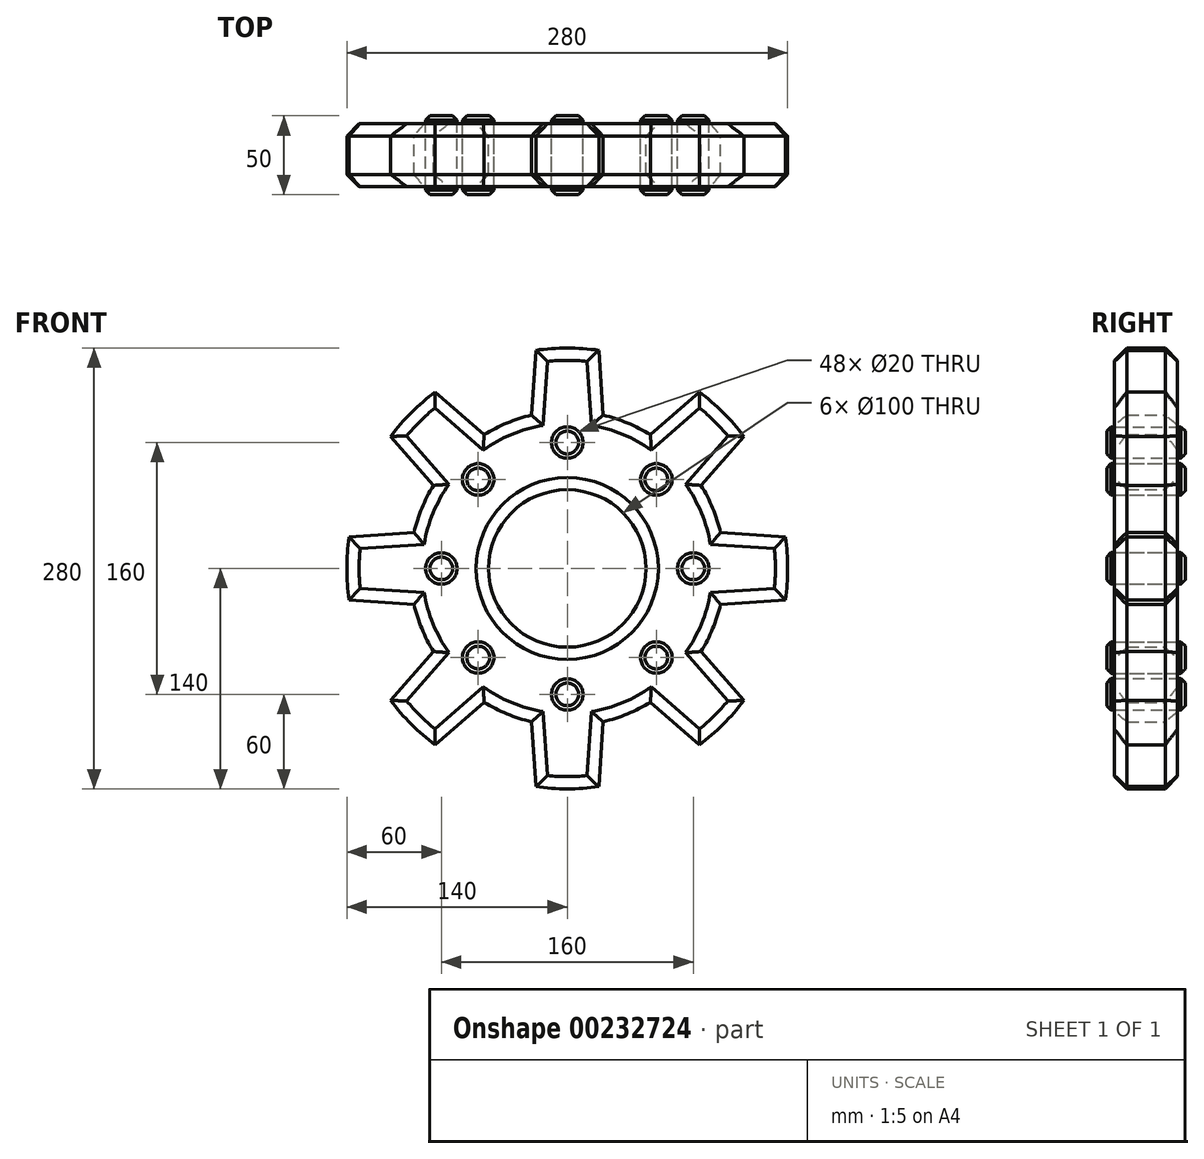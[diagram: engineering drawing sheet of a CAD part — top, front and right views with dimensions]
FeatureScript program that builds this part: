
annotation { "Feature Type Name" : "Feature", "Feature Type Description" : "" }
export const myFeature = defineFeature(function(context is Context, id is Id, definition is map)
    precondition{}
    {
        {
            var Q0;
            Q0=qCreatedBy(makeId("Front.planeOp"),FACE);
            var sketch = newSketch(context, id + "F0", { "sketchPlane" : qUnion([Q0])});
            skLineSegment(sketch, "E0.bottom", {"start": v(-160, 160) * mm, "end": v(160, 160) * mm});
            skLineSegment(sketch, "E0.top", {"start": v(-160, -160) * mm, "end": v(160, -160) * mm});
            skLineSegment(sketch, "E0.left", {"start": v(-160, 160) * mm, "end": v(-160, -160) * mm});
            skLineSegment(sketch, "E0.right", {"start": v(160, 160) * mm, "end": v(160, -160) * mm});
            skPoint(sketch, "E0.middle", {"position": v(0, 0) * mm});
            skLineSegment(sketch, "E1.bottom", {"start": v(-40, 160) * mm, "end": v(40, 160) * mm});
            skLineSegment(sketch, "E1.top", {"start": v(-40, -160) * mm, "end": v(40, -160) * mm});
            skLineSegment(sketch, "E1.left", {"start": v(-40, 160) * mm, "end": v(-40, -160) * mm});
            skLineSegment(sketch, "E1.right", {"start": v(40, 160) * mm, "end": v(40, -160) * mm});
            skLineSegment(sketch, "E2.bottom", {"start": v(-20, 160) * mm, "end": v(20, 160) * mm});
            skLineSegment(sketch, "E2.top", {"start": v(-20, -160) * mm, "end": v(20, -160) * mm});
            skLineSegment(sketch, "E2.left", {"start": v(-20, 160) * mm, "end": v(-20, -160) * mm});
            skLineSegment(sketch, "E2.right", {"start": v(20, 160) * mm, "end": v(20, -160) * mm});
            skLineSegment(sketch, "E3.bottom", {"start": v(-160, 40) * mm, "end": v(160, 40) * mm});
            skLineSegment(sketch, "E3.top", {"start": v(-160, -40) * mm, "end": v(160, -40) * mm});
            skLineSegment(sketch, "E3.left", {"start": v(-160, 40) * mm, "end": v(-160, -40) * mm});
            skLineSegment(sketch, "E3.right", {"start": v(160, 40) * mm, "end": v(160, -40) * mm});
            skLineSegment(sketch, "E4.bottom", {"start": v(-160, 20) * mm, "end": v(160, 20) * mm});
            skLineSegment(sketch, "E4.top", {"start": v(-160, -20) * mm, "end": v(160, -20) * mm});
            skLineSegment(sketch, "E4.left", {"start": v(-160, 20) * mm, "end": v(-160, -20) * mm});
            skLineSegment(sketch, "E4.right", {"start": v(160, 20) * mm, "end": v(160, -20) * mm});
            skLineSegment(sketch, "E5", {"start": v(-160, 160) * mm, "end": v(160, -160) * mm});
            skLineSegment(sketch, "E6", {"start": v(-160, -160) * mm, "end": v(160, 160) * mm});
            skLineSegment(sketch, "E7", {"start": v(-84.85, 141.42) * mm, "end": v(-113.14, 113.14) * mm});
            skLineSegment(sketch, "E8", {"start": v(-113.14, 113.14) * mm, "end": v(-141.42, 84.85) * mm});
            skLineSegment(sketch, "E9", {"start": v(0, 0) * mm, "end": v(-113.14, 113.14) * mm});
            skLineSegment(sketch, "E10", {"start": v(84.85, -141.42) * mm, "end": v(113.14, -113.14) * mm});
            skLineSegment(sketch, "E11", {"start": v(113.14, -113.14) * mm, "end": v(141.42, -84.85) * mm});
            skLineSegment(sketch, "E12", {"start": v(0, 0) * mm, "end": v(113.14, -113.14) * mm});
            skPoint(sketch, "E13", {"position": v(-99, 127.28) * mm});
            skPoint(sketch, "E14", {"position": v(-127.28, 99) * mm});
            skPoint(sketch, "E15", {"position": v(127.28, -99) * mm});
            skPoint(sketch, "E16", {"position": v(99, -127.28) * mm});
            skLineSegment(sketch, "E17", {"start": v(-127.28, 99) * mm, "end": v(99, -127.28) * mm});
            skLineSegment(sketch, "E18", {"start": v(-99, 127.28) * mm, "end": v(127.28, -99) * mm});
            skLineSegment(sketch, "E19", {"start": v(-160, 0) * mm, "end": v(160, 0) * mm});
            skLineSegment(sketch, "E20", {"start": v(0, 160) * mm, "end": v(0, -160) * mm});
            skLineSegment(sketch, "E21", {"start": v(84.85, 141.42) * mm, "end": v(113.14, 113.14) * mm});
            skLineSegment(sketch, "E22", {"start": v(113.14, 113.14) * mm, "end": v(141.42, 84.85) * mm});
            skPoint(sketch, "E23", {"position": v(99, 127.28) * mm});
            skPoint(sketch, "E24", {"position": v(127.28, 99) * mm});
            skLineSegment(sketch, "E25", {"start": v(-141.42, -84.85) * mm, "end": v(-113.14, -113.14) * mm});
            skLineSegment(sketch, "E26", {"start": v(-113.14, -113.14) * mm, "end": v(-84.85, -141.42) * mm});
            skPoint(sketch, "E27", {"position": v(-127.28, -99) * mm});
            skPoint(sketch, "E28", {"position": v(-99, -127.28) * mm});
            skLineSegment(sketch, "E29", {"start": v(-127.28, -99) * mm, "end": v(99, 127.28) * mm});
            skLineSegment(sketch, "E30", {"start": v(-99, -127.28) * mm, "end": v(127.28, 99) * mm});
            skCircle(sketch, "E31", {"center": v(0, 0) * mm, "radius": 80 * mm});
            skPoint(sketch, "E32", {"position": v(0, 80) * mm});
            skPoint(sketch, "E33", {"position": v(56.57, 56.57) * mm});
            skPoint(sketch, "E34", {"position": v(-56.57, 56.57) * mm});
            skPoint(sketch, "E35", {"position": v(-80, 0) * mm});
            skPoint(sketch, "E36", {"position": v(80, 0) * mm});
            skPoint(sketch, "E37", {"position": v(0, -80) * mm});
            skPoint(sketch, "E38", {"position": v(-56.57, -56.57) * mm});
            skPoint(sketch, "E39", {"position": v(56.57, -56.57) * mm});
            skSolve(sketch);
        }
        {
            var Q0;
            Q0=qCreatedBy(makeId("Front.planeOp"),FACE);
            var sketch = newSketch(context, id + "F1", { "sketchPlane" : qUnion([Q0])});
            skCircle(sketch, "E40", {"center": v(0, 0) * mm, "radius": 50 * mm});
            skArc(sketch, "E41", {"start": v(20, 138.56) * mm, "mid": v(0, 140) * mm, "end": v(-20, 138.56) * mm});
            skArc(sketch, "E42", {"start": v(-83.84, 112.12) * mm, "mid": v(-99, 99) * mm, "end": v(-112.12, 83.84) * mm});
            skArc(sketch, "E43", {"start": v(-138.56, 20) * mm, "mid": v(-140, 0) * mm, "end": v(-138.56, -20) * mm});
            skArc(sketch, "E44", {"start": v(-112.12, -83.84) * mm, "mid": v(-99, -99) * mm, "end": v(-83.84, -112.12) * mm});
            skArc(sketch, "E45", {"start": v(-20, -138.56) * mm, "mid": v(0, -140) * mm, "end": v(20, -138.56) * mm});
            skArc(sketch, "E46", {"start": v(83.84, -112.12) * mm, "mid": v(99, -99) * mm, "end": v(112.12, -83.84) * mm});
            skArc(sketch, "E47", {"start": v(138.56, -20) * mm, "mid": v(140, 0) * mm, "end": v(138.56, 20) * mm});
            skArc(sketch, "E48", {"start": v(112.12, 83.84) * mm, "mid": v(99, 99) * mm, "end": v(83.84, 112.12) * mm});
            skLineSegment(sketch, "E49", {"start": v(-20, 138.56) * mm, "end": v(-22.76, 97.38) * mm});
            skLineSegment(sketch, "E50", {"start": v(20, 138.56) * mm, "end": v(22.76, 97.38) * mm});
            skArc(sketch, "E51", {"start": v(-22.76, 97.38) * mm, "mid": v(-38.27, 92.39) * mm, "end": v(-52.76, 84.95) * mm});
            skLineSegment(sketch, "E52", {"start": v(-112.12, 83.84) * mm, "end": v(-84.95, 52.76) * mm});
            skLineSegment(sketch, "E53", {"start": v(-83.84, 112.12) * mm, "end": v(-52.76, 84.95) * mm});
            skArc(sketch, "E54", {"start": v(-84.95, 52.76) * mm, "mid": v(-92.39, 38.27) * mm, "end": v(-97.38, 22.76) * mm});
            skLineSegment(sketch, "E55", {"start": v(-138.56, 20) * mm, "end": v(-97.38, 22.76) * mm});
            skLineSegment(sketch, "E56", {"start": v(-138.56, -20) * mm, "end": v(-97.38, -22.76) * mm});
            skArc(sketch, "E57", {"start": v(-97.38, -22.76) * mm, "mid": v(-92.39, -38.27) * mm, "end": v(-84.95, -52.76) * mm});
            skLineSegment(sketch, "E58", {"start": v(-112.12, -83.84) * mm, "end": v(-84.95, -52.76) * mm});
            skLineSegment(sketch, "E59", {"start": v(-83.84, -112.12) * mm, "end": v(-52.76, -84.95) * mm});
            skArc(sketch, "E60", {"start": v(-52.76, -84.95) * mm, "mid": v(-38.27, -92.39) * mm, "end": v(-22.76, -97.38) * mm});
            skLineSegment(sketch, "E61", {"start": v(-20, -138.56) * mm, "end": v(-22.76, -97.38) * mm});
            skLineSegment(sketch, "E62", {"start": v(20, -138.56) * mm, "end": v(22.76, -97.38) * mm});
            skArc(sketch, "E63", {"start": v(22.76, -97.38) * mm, "mid": v(38.27, -92.39) * mm, "end": v(52.76, -84.95) * mm});
            skLineSegment(sketch, "E64", {"start": v(138.56, 20) * mm, "end": v(97.38, 22.76) * mm});
            skLineSegment(sketch, "E65", {"start": v(138.56, -20) * mm, "end": v(97.38, -22.76) * mm});
            skArc(sketch, "E66", {"start": v(97.38, 22.76) * mm, "mid": v(92.39, 38.27) * mm, "end": v(84.95, 52.76) * mm});
            skLineSegment(sketch, "E67", {"start": v(83.84, 112.12) * mm, "end": v(52.76, 84.95) * mm});
            skLineSegment(sketch, "E68", {"start": v(112.12, 83.84) * mm, "end": v(84.95, 52.76) * mm});
            skArc(sketch, "E69", {"start": v(52.76, 84.95) * mm, "mid": v(38.27, 92.39) * mm, "end": v(22.76, 97.38) * mm});
            skLineSegment(sketch, "E70", {"start": v(112.12, -83.84) * mm, "end": v(84.95, -52.76) * mm});
            skLineSegment(sketch, "E71", {"start": v(83.84, -112.12) * mm, "end": v(52.76, -84.95) * mm});
            skArc(sketch, "E72", {"start": v(84.95, -52.76) * mm, "mid": v(92.39, -38.27) * mm, "end": v(97.38, -22.76) * mm});
            skCircle(sketch, "E73", {"center": v(0, 80) * mm, "radius": 10 * mm});
            skCircle(sketch, "E74", {"center": v(56.57, 56.57) * mm, "radius": 10 * mm});
            skCircle(sketch, "E75", {"center": v(-56.57, 56.57) * mm, "radius": 10 * mm});
            skCircle(sketch, "E76", {"center": v(-80, 0) * mm, "radius": 10 * mm});
            skCircle(sketch, "E77", {"center": v(-56.57, -56.57) * mm, "radius": 10 * mm});
            skCircle(sketch, "E78", {"center": v(0, -80) * mm, "radius": 10 * mm});
            skCircle(sketch, "E79", {"center": v(56.57, -56.57) * mm, "radius": 10 * mm});
            skCircle(sketch, "E80", {"center": v(80, 0) * mm, "radius": 10 * mm});
            skSolve(sketch);
        }
        {
            var Q0;
            Q0=makeQuery(id+"F1.imprint","IMPRINT",FACE,{"disambiguationData":[TD([[makeQuery(id+"F1.imprint","IMPRINT",EDGE,{"derivedFrom":sQuery(id+"F1.wireOp",EDGE,"E40")}),-1.0]])]});
            extrude(context, id + "F2", {"entities" : qUnion([Q0]), "endBound" : BoundingType.SYMMETRIC, "depth" : 40 * mm});
        }
        {
            var Q0;
            Q0=makeQuery(id+"F1.imprint","IMPRINT",FACE,{"disambiguationData":[TD([[makeQuery(id+"F1.imprint","IMPRINT",EDGE,{"derivedFrom":sQuery(id+"F1.wireOp",EDGE,"E75")}),1.0]])]});
            var Q1;
            Q1=makeQuery(id+"F1.imprint","IMPRINT",FACE,{"disambiguationData":[TD([[makeQuery(id+"F1.imprint","IMPRINT",EDGE,{"derivedFrom":sQuery(id+"F1.wireOp",EDGE,"E76")}),1.0]])]});
            var Q2;
            Q2=makeQuery(id+"F1.imprint","IMPRINT",FACE,{"disambiguationData":[TD([[makeQuery(id+"F1.imprint","IMPRINT",EDGE,{"derivedFrom":sQuery(id+"F1.wireOp",EDGE,"E77")}),1.0]])]});
            var Q3;
            Q3=makeQuery(id+"F1.imprint","IMPRINT",FACE,{"disambiguationData":[TD([[makeQuery(id+"F1.imprint","IMPRINT",EDGE,{"derivedFrom":sQuery(id+"F1.wireOp",EDGE,"E78")}),1.0]])]});
            var Q4;
            Q4=makeQuery(id+"F1.imprint","IMPRINT",FACE,{"disambiguationData":[TD([[makeQuery(id+"F1.imprint","IMPRINT",EDGE,{"derivedFrom":sQuery(id+"F1.wireOp",EDGE,"E79")}),1.0]])]});
            var Q5;
            Q5=makeQuery(id+"F1.imprint","IMPRINT",FACE,{"disambiguationData":[TD([[makeQuery(id+"F1.imprint","IMPRINT",EDGE,{"derivedFrom":sQuery(id+"F1.wireOp",EDGE,"E80")}),1.0]])]});
            var Q6;
            Q6=makeQuery(id+"F1.imprint","IMPRINT",FACE,{"disambiguationData":[TD([[makeQuery(id+"F1.imprint","IMPRINT",EDGE,{"derivedFrom":sQuery(id+"F1.wireOp",EDGE,"E74")}),1.0]])]});
            var Q7;
            Q7=makeQuery(id+"F1.imprint","IMPRINT",FACE,{"disambiguationData":[TD([[makeQuery(id+"F1.imprint","IMPRINT",EDGE,{"derivedFrom":sQuery(id+"F1.wireOp",EDGE,"E73")}),1.0]])]});
            extrude(context, id + "F3", {"entities" : qUnion([Q0, Q1, Q2, Q3, Q4, Q5, Q6, Q7]), "endBound" : BoundingType.SYMMETRIC, "depth" : 50 * mm});
        }
        {
            var Q0;
            Q0=makeQuery(id+"F2.opExtrude","CAP_EDGE",EDGE,{"disambiguationData":[OSD([sQuery(id+"F1.wireOp",EDGE,"E41")])],"isStart":false});
            var Q1;
            Q1=makeQuery(id+"F2.opExtrude","CAP_EDGE",EDGE,{"disambiguationData":[OSD([sQuery(id+"F1.wireOp",EDGE,"E49")])],"isStart":false});
            var Q2;
            Q2=makeQuery(id+"F2.opExtrude","CAP_EDGE",EDGE,{"disambiguationData":[OSD([sQuery(id+"F1.wireOp",EDGE,"E50")])],"isStart":false});
            var Q3;
            Q3=makeQuery(id+"F2.opExtrude","CAP_EDGE",EDGE,{"disambiguationData":[OSD([sQuery(id+"F1.wireOp",EDGE,"E69")])],"isStart":false});
            var Q4;
            Q4=makeQuery(id+"F2.opExtrude","CAP_EDGE",EDGE,{"disambiguationData":[OSD([sQuery(id+"F1.wireOp",EDGE,"E67")])],"isStart":false});
            var Q5;
            Q5=makeQuery(id+"F2.opExtrude","CAP_EDGE",EDGE,{"disambiguationData":[OSD([sQuery(id+"F1.wireOp",EDGE,"E68")])],"isStart":false});
            var Q6;
            Q6=makeQuery(id+"F2.opExtrude","CAP_EDGE",EDGE,{"disambiguationData":[OSD([sQuery(id+"F1.wireOp",EDGE,"E66")])],"isStart":false});
            var Q7;
            Q7=makeQuery(id+"F2.opExtrude","CAP_EDGE",EDGE,{"disambiguationData":[OSD([sQuery(id+"F1.wireOp",EDGE,"E64")])],"isStart":false});
            var Q8;
            Q8=makeQuery(id+"F2.opExtrude","CAP_EDGE",EDGE,{"disambiguationData":[OSD([sQuery(id+"F1.wireOp",EDGE,"E47")])],"isStart":false});
            var Q9;
            Q9=makeQuery(id+"F2.opExtrude","CAP_EDGE",EDGE,{"disambiguationData":[OSD([sQuery(id+"F1.wireOp",EDGE,"E48")])],"isStart":false});
            var Q10;
            Q10=makeQuery(id+"F2.opExtrude","CAP_EDGE",EDGE,{"disambiguationData":[OSD([sQuery(id+"F1.wireOp",EDGE,"E65")])],"isStart":false});
            var Q11;
            Q11=makeQuery(id+"F2.opExtrude","CAP_EDGE",EDGE,{"disambiguationData":[OSD([sQuery(id+"F1.wireOp",EDGE,"E72")])],"isStart":false});
            var Q12;
            Q12=makeQuery(id+"F2.opExtrude","CAP_EDGE",EDGE,{"disambiguationData":[OSD([sQuery(id+"F1.wireOp",EDGE,"E46")])],"isStart":false});
            var Q13;
            Q13=makeQuery(id+"F2.opExtrude","CAP_EDGE",EDGE,{"disambiguationData":[OSD([sQuery(id+"F1.wireOp",EDGE,"E71")])],"isStart":false});
            var Q14;
            Q14=makeQuery(id+"F2.opExtrude","CAP_EDGE",EDGE,{"disambiguationData":[OSD([sQuery(id+"F1.wireOp",EDGE,"E63")])],"isStart":false});
            var Q15;
            Q15=makeQuery(id+"F2.opExtrude","CAP_EDGE",EDGE,{"disambiguationData":[OSD([sQuery(id+"F1.wireOp",EDGE,"E62")])],"isStart":false});
            var Q16;
            Q16=makeQuery(id+"F2.opExtrude","CAP_EDGE",EDGE,{"disambiguationData":[OSD([sQuery(id+"F1.wireOp",EDGE,"E45")])],"isStart":false});
            var Q17;
            Q17=makeQuery(id+"F2.opExtrude","CAP_EDGE",EDGE,{"disambiguationData":[OSD([sQuery(id+"F1.wireOp",EDGE,"E60")])],"isStart":false});
            var Q18;
            Q18=makeQuery(id+"F2.opExtrude","CAP_EDGE",EDGE,{"disambiguationData":[OSD([sQuery(id+"F1.wireOp",EDGE,"E59")])],"isStart":false});
            var Q19;
            Q19=makeQuery(id+"F2.opExtrude","CAP_EDGE",EDGE,{"disambiguationData":[OSD([sQuery(id+"F1.wireOp",EDGE,"E70")])],"isStart":false});
            var Q20;
            Q20=makeQuery(id+"F2.opExtrude","CAP_EDGE",EDGE,{"disambiguationData":[OSD([sQuery(id+"F1.wireOp",EDGE,"E51")])],"isStart":false});
            var Q21;
            Q21=makeQuery(id+"F2.opExtrude","CAP_EDGE",EDGE,{"disambiguationData":[OSD([sQuery(id+"F1.wireOp",EDGE,"E53")])],"isStart":false});
            var Q22;
            Q22=makeQuery(id+"F2.opExtrude","CAP_EDGE",EDGE,{"disambiguationData":[OSD([sQuery(id+"F1.wireOp",EDGE,"E42")])],"isStart":false});
            var Q23;
            Q23=makeQuery(id+"F2.opExtrude","CAP_EDGE",EDGE,{"disambiguationData":[OSD([sQuery(id+"F1.wireOp",EDGE,"E52")])],"isStart":false});
            var Q24;
            Q24=makeQuery(id+"F2.opExtrude","CAP_EDGE",EDGE,{"disambiguationData":[OSD([sQuery(id+"F1.wireOp",EDGE,"E54")])],"isStart":false});
            var Q25;
            Q25=makeQuery(id+"F2.opExtrude","CAP_EDGE",EDGE,{"disambiguationData":[OSD([sQuery(id+"F1.wireOp",EDGE,"E55")])],"isStart":false});
            var Q26;
            Q26=makeQuery(id+"F2.opExtrude","CAP_EDGE",EDGE,{"disambiguationData":[OSD([sQuery(id+"F1.wireOp",EDGE,"E43")])],"isStart":false});
            var Q27;
            Q27=makeQuery(id+"F2.opExtrude","CAP_EDGE",EDGE,{"disambiguationData":[OSD([sQuery(id+"F1.wireOp",EDGE,"E56")])],"isStart":false});
            var Q28;
            Q28=makeQuery(id+"F2.opExtrude","CAP_EDGE",EDGE,{"disambiguationData":[OSD([sQuery(id+"F1.wireOp",EDGE,"E57")])],"isStart":false});
            var Q29;
            Q29=makeQuery(id+"F2.opExtrude","CAP_EDGE",EDGE,{"disambiguationData":[OSD([sQuery(id+"F1.wireOp",EDGE,"E58")])],"isStart":false});
            var Q30;
            Q30=makeQuery(id+"F2.opExtrude","CAP_EDGE",EDGE,{"disambiguationData":[OSD([sQuery(id+"F1.wireOp",EDGE,"E44")])],"isStart":false});
            var Q31;
            Q31=makeQuery(id+"F2.opExtrude","CAP_EDGE",EDGE,{"disambiguationData":[OSD([sQuery(id+"F1.wireOp",EDGE,"E42")])],"isStart":true});
            var Q32;
            Q32=makeQuery(id+"F2.opExtrude","CAP_EDGE",EDGE,{"disambiguationData":[OSD([sQuery(id+"F1.wireOp",EDGE,"E52")])],"isStart":true});
            var Q33;
            Q33=makeQuery(id+"F2.opExtrude","CAP_EDGE",EDGE,{"disambiguationData":[OSD([sQuery(id+"F1.wireOp",EDGE,"E54")])],"isStart":true});
            var Q34;
            Q34=makeQuery(id+"F2.opExtrude","CAP_EDGE",EDGE,{"disambiguationData":[OSD([sQuery(id+"F1.wireOp",EDGE,"E55")])],"isStart":true});
            var Q35;
            Q35=makeQuery(id+"F2.opExtrude","CAP_EDGE",EDGE,{"disambiguationData":[OSD([sQuery(id+"F1.wireOp",EDGE,"E43")])],"isStart":true});
            var Q36;
            Q36=makeQuery(id+"F2.opExtrude","CAP_EDGE",EDGE,{"disambiguationData":[OSD([sQuery(id+"F1.wireOp",EDGE,"E56")])],"isStart":true});
            var Q37;
            Q37=makeQuery(id+"F2.opExtrude","CAP_EDGE",EDGE,{"disambiguationData":[OSD([sQuery(id+"F1.wireOp",EDGE,"E57")])],"isStart":true});
            var Q38;
            Q38=makeQuery(id+"F2.opExtrude","CAP_EDGE",EDGE,{"disambiguationData":[OSD([sQuery(id+"F1.wireOp",EDGE,"E58")])],"isStart":true});
            var Q39;
            Q39=makeQuery(id+"F2.opExtrude","CAP_EDGE",EDGE,{"disambiguationData":[OSD([sQuery(id+"F1.wireOp",EDGE,"E44")])],"isStart":true});
            var Q40;
            Q40=makeQuery(id+"F2.opExtrude","CAP_EDGE",EDGE,{"disambiguationData":[OSD([sQuery(id+"F1.wireOp",EDGE,"E59")])],"isStart":true});
            var Q41;
            Q41=makeQuery(id+"F2.opExtrude","CAP_EDGE",EDGE,{"disambiguationData":[OSD([sQuery(id+"F1.wireOp",EDGE,"E60")])],"isStart":true});
            var Q42;
            Q42=makeQuery(id+"F2.opExtrude","CAP_EDGE",EDGE,{"disambiguationData":[OSD([sQuery(id+"F1.wireOp",EDGE,"E61")])],"isStart":true});
            var Q43;
            Q43=makeQuery(id+"F2.opExtrude","CAP_EDGE",EDGE,{"disambiguationData":[OSD([sQuery(id+"F1.wireOp",EDGE,"E45")])],"isStart":true});
            var Q44;
            Q44=makeQuery(id+"F2.opExtrude","CAP_EDGE",EDGE,{"disambiguationData":[OSD([sQuery(id+"F1.wireOp",EDGE,"E62")])],"isStart":true});
            var Q45;
            Q45=makeQuery(id+"F2.opExtrude","CAP_EDGE",EDGE,{"disambiguationData":[OSD([sQuery(id+"F1.wireOp",EDGE,"E63")])],"isStart":true});
            var Q46;
            Q46=makeQuery(id+"F2.opExtrude","CAP_EDGE",EDGE,{"disambiguationData":[OSD([sQuery(id+"F1.wireOp",EDGE,"E71")])],"isStart":true});
            var Q47;
            Q47=makeQuery(id+"F2.opExtrude","CAP_EDGE",EDGE,{"disambiguationData":[OSD([sQuery(id+"F1.wireOp",EDGE,"E46")])],"isStart":true});
            var Q48;
            Q48=makeQuery(id+"F2.opExtrude","CAP_EDGE",EDGE,{"disambiguationData":[OSD([sQuery(id+"F1.wireOp",EDGE,"E70")])],"isStart":true});
            var Q49;
            Q49=makeQuery(id+"F2.opExtrude","CAP_EDGE",EDGE,{"disambiguationData":[OSD([sQuery(id+"F1.wireOp",EDGE,"E72")])],"isStart":true});
            var Q50;
            Q50=makeQuery(id+"F2.opExtrude","CAP_EDGE",EDGE,{"disambiguationData":[OSD([sQuery(id+"F1.wireOp",EDGE,"E65")])],"isStart":true});
            var Q51;
            Q51=makeQuery(id+"F2.opExtrude","CAP_EDGE",EDGE,{"disambiguationData":[OSD([sQuery(id+"F1.wireOp",EDGE,"E47")])],"isStart":true});
            var Q52;
            Q52=makeQuery(id+"F2.opExtrude","CAP_EDGE",EDGE,{"disambiguationData":[OSD([sQuery(id+"F1.wireOp",EDGE,"E64")])],"isStart":true});
            var Q53;
            Q53=makeQuery(id+"F2.opExtrude","CAP_EDGE",EDGE,{"disambiguationData":[OSD([sQuery(id+"F1.wireOp",EDGE,"E66")])],"isStart":true});
            var Q54;
            Q54=makeQuery(id+"F2.opExtrude","CAP_EDGE",EDGE,{"disambiguationData":[OSD([sQuery(id+"F1.wireOp",EDGE,"E68")])],"isStart":true});
            var Q55;
            Q55=makeQuery(id+"F2.opExtrude","CAP_EDGE",EDGE,{"disambiguationData":[OSD([sQuery(id+"F1.wireOp",EDGE,"E48")])],"isStart":true});
            var Q56;
            Q56=makeQuery(id+"F2.opExtrude","CAP_EDGE",EDGE,{"disambiguationData":[OSD([sQuery(id+"F1.wireOp",EDGE,"E67")])],"isStart":true});
            var Q57;
            Q57=makeQuery(id+"F2.opExtrude","CAP_EDGE",EDGE,{"disambiguationData":[OSD([sQuery(id+"F1.wireOp",EDGE,"E69")])],"isStart":true});
            var Q58;
            Q58=makeQuery(id+"F2.opExtrude","CAP_EDGE",EDGE,{"disambiguationData":[OSD([sQuery(id+"F1.wireOp",EDGE,"E50")])],"isStart":true});
            var Q59;
            Q59=makeQuery(id+"F2.opExtrude","CAP_EDGE",EDGE,{"disambiguationData":[OSD([sQuery(id+"F1.wireOp",EDGE,"E41")])],"isStart":true});
            var Q60;
            Q60=makeQuery(id+"F2.opExtrude","CAP_EDGE",EDGE,{"disambiguationData":[OSD([sQuery(id+"F1.wireOp",EDGE,"E49")])],"isStart":true});
            var Q61;
            Q61=makeQuery(id+"F2.opExtrude","CAP_EDGE",EDGE,{"disambiguationData":[OSD([sQuery(id+"F1.wireOp",EDGE,"E51")])],"isStart":true});
            var Q62;
            Q62=makeQuery(id+"F2.opExtrude","CAP_EDGE",EDGE,{"disambiguationData":[OSD([sQuery(id+"F1.wireOp",EDGE,"E53")])],"isStart":true});
            var Q63;
            Q63=makeQuery(id+"F2.opExtrude","CAP_EDGE",EDGE,{"disambiguationData":[OSD([sQuery(id+"F1.wireOp",EDGE,"E40")])],"isStart":true});
            var Q64;
            Q64=makeQuery(id+"F2.opExtrude","CAP_EDGE",EDGE,{"disambiguationData":[OSD([sQuery(id+"F1.wireOp",EDGE,"E40")])],"isStart":false});
            var Q65;
            Q65=makeQuery(id+"F2.opExtrude","CAP_EDGE",EDGE,{"disambiguationData":[OSD([sQuery(id+"F1.wireOp",EDGE,"E61")])],"isStart":false});
            chamfer(context, id + "F4", {"entities" : qUnion([Q0, Q1, Q2, Q3, Q4, Q5, Q6, Q7, Q8, Q9, Q10, Q11, Q12, Q13, Q14, Q15, Q16, Q17, Q18, Q19, Q20, Q21, Q22, Q23, Q24, Q25, Q26, Q27, Q28, Q29, Q30, Q31, Q32, Q33, Q34, Q35, Q36, Q37, Q38, Q39, Q40, Q41, Q42, Q43, Q44, Q45, Q46, Q47, Q48, Q49, Q50, Q51, Q52, Q53, Q54, Q55, Q56, Q57, Q58, Q59, Q60, Q61, Q62, Q63, Q64, Q65]), "width" : 7.8 * mm, "tangentPropagation" : true});
        }
        {
            var Q0;
            Q0=makeQuery(id+"F3.opExtrude","CAP_EDGE",EDGE,{"disambiguationData":[OSD([sQuery(id+"F1.wireOp",EDGE,"E75")])],"isStart":false});
            var Q1;
            Q1=makeQuery(id+"F3.opExtrude","CAP_EDGE",EDGE,{"disambiguationData":[OSD([sQuery(id+"F1.wireOp",EDGE,"E73")])],"isStart":false});
            var Q2;
            Q2=makeQuery(id+"F3.opExtrude","CAP_EDGE",EDGE,{"disambiguationData":[OSD([sQuery(id+"F1.wireOp",EDGE,"E74")])],"isStart":false});
            var Q3;
            Q3=makeQuery(id+"F3.opExtrude","CAP_EDGE",EDGE,{"disambiguationData":[OSD([sQuery(id+"F1.wireOp",EDGE,"E80")])],"isStart":false});
            var Q4;
            Q4=makeQuery(id+"F3.opExtrude","CAP_EDGE",EDGE,{"disambiguationData":[OSD([sQuery(id+"F1.wireOp",EDGE,"E76")])],"isStart":false});
            var Q5;
            Q5=makeQuery(id+"F3.opExtrude","CAP_EDGE",EDGE,{"disambiguationData":[OSD([sQuery(id+"F1.wireOp",EDGE,"E77")])],"isStart":false});
            var Q6;
            Q6=makeQuery(id+"F3.opExtrude","CAP_EDGE",EDGE,{"disambiguationData":[OSD([sQuery(id+"F1.wireOp",EDGE,"E78")])],"isStart":false});
            var Q7;
            Q7=makeQuery(id+"F3.opExtrude","CAP_EDGE",EDGE,{"disambiguationData":[OSD([sQuery(id+"F1.wireOp",EDGE,"E79")])],"isStart":false});
            var Q8;
            Q8=makeQuery(id+"F3.opExtrude","CAP_EDGE",EDGE,{"disambiguationData":[OSD([sQuery(id+"F1.wireOp",EDGE,"E75")])],"isStart":true});
            var Q9;
            Q9=makeQuery(id+"F3.opExtrude","CAP_EDGE",EDGE,{"disambiguationData":[OSD([sQuery(id+"F1.wireOp",EDGE,"E73")])],"isStart":true});
            var Q10;
            Q10=makeQuery(id+"F3.opExtrude","CAP_EDGE",EDGE,{"disambiguationData":[OSD([sQuery(id+"F1.wireOp",EDGE,"E76")])],"isStart":true});
            var Q11;
            Q11=makeQuery(id+"F3.opExtrude","CAP_EDGE",EDGE,{"disambiguationData":[OSD([sQuery(id+"F1.wireOp",EDGE,"E74")])],"isStart":true});
            var Q12;
            Q12=makeQuery(id+"F3.opExtrude","CAP_EDGE",EDGE,{"disambiguationData":[OSD([sQuery(id+"F1.wireOp",EDGE,"E77")])],"isStart":true});
            var Q13;
            Q13=makeQuery(id+"F3.opExtrude","CAP_EDGE",EDGE,{"disambiguationData":[OSD([sQuery(id+"F1.wireOp",EDGE,"E78")])],"isStart":true});
            var Q14;
            Q14=makeQuery(id+"F3.opExtrude","CAP_EDGE",EDGE,{"disambiguationData":[OSD([sQuery(id+"F1.wireOp",EDGE,"E79")])],"isStart":true});
            var Q15;
            Q15=makeQuery(id+"F3.opExtrude","CAP_EDGE",EDGE,{"disambiguationData":[OSD([sQuery(id+"F1.wireOp",EDGE,"E80")])],"isStart":true});
            chamfer(context, id + "F5", {"entities" : qUnion([Q0, Q1, Q2, Q3, Q4, Q5, Q6, Q7, Q8, Q9, Q10, Q11, Q12, Q13, Q14, Q15]), "width" : 2.8 * mm, "tangentPropagation" : true});
        }
    });
